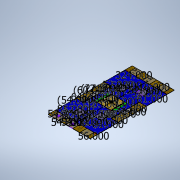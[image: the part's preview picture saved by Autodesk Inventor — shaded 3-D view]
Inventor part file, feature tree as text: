
AUTODESK INVENTOR PART (.ipt)
format: ipt  version: 2020 (Build 240168000, 168)  size: 259,584 bytes
history: native  units: in
note: dims shown in document units (in); Inventor stores cm internally (conversion verified against a paired STEP export)
features: sketch x1, other x1
ambient origin geometry x8: Origin, YZ Plane, XZ Plane, XY Plane, X Axis, Y Axis, Z Axis, Center Point
feature tree (2):
  sketch  "Sketch1"  dims[d0=324.0in d1=648.0in d25=56.0in d34=52.0in d35=52.0in d60=52.0in d61=52.0in d71=52.0in d72=52.0in d77=108.0in d78=110.0in d82=54.0in d83=108.0in d85=110.0in d87=81.0in d93=110.0in d95=81.0in d97=52.0in d99=52.0in d102=54.0in d103=54.0in d105=54.0in d111=3.0in d112=3.0in d113=27.0in d114=30.0in d124=216.0in d126=54.0in d127=108.0in d129=81.0in d134=27.0in d136=60.0in]
  other  "Image2"
